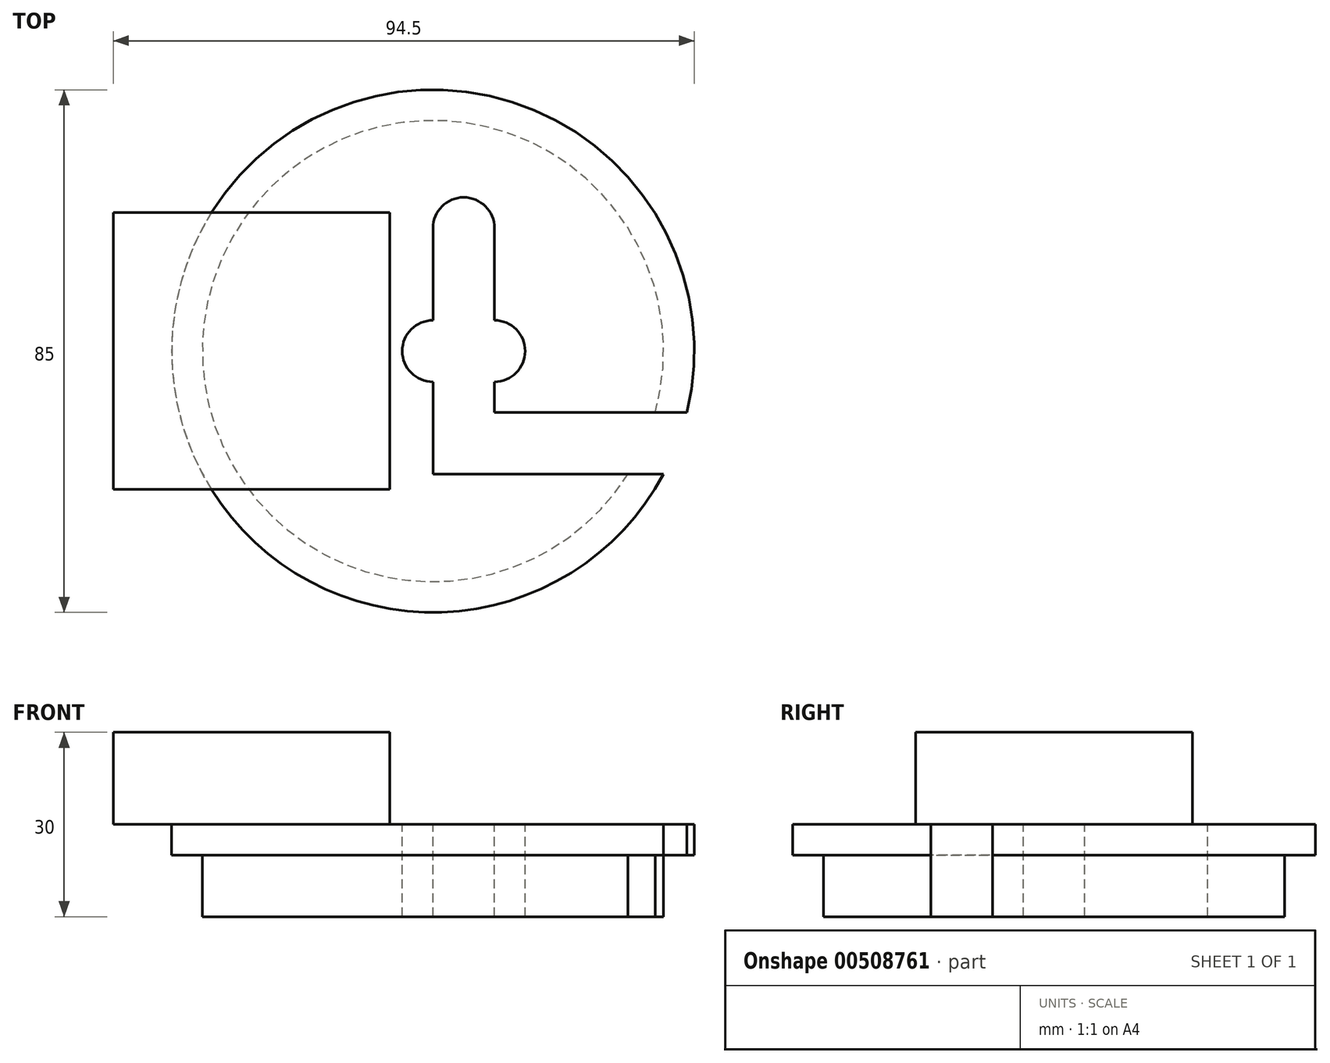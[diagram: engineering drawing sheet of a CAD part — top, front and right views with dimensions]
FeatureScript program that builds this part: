
annotation { "Feature Type Name" : "Feature", "Feature Type Description" : "" }
export const myFeature = defineFeature(function(context is Context, id is Id, definition is map)
    precondition{}
    {
        {
            var Q0;
            Q0=qCreatedBy(makeId("Top.planeOp"),FACE);
            var sketch = newSketch(context, id + "F0", { "sketchPlane" : qUnion([Q0])});
            skArc(sketch, "E0", {"start": v(41.3, -10) * mm, "mid": v(-39.72, 15.12) * mm, "end": v(37.5, -20) * mm});
            skArc(sketch, "E1", {"start": v(0, 5) * mm, "mid": v(-5, 0) * mm, "end": v(0, -5) * mm});
            skLineSegment(sketch, "E2", {"start": v(0, 5) * mm, "end": v(0, 20) * mm});
            skArc(sketch, "E3", {"start": v(10, 20) * mm, "mid": v(5, 25) * mm, "end": v(0, 20) * mm});
            skLineSegment(sketch, "E4", {"start": v(10, 20) * mm, "end": v(10, 5) * mm});
            skArc(sketch, "E5", {"start": v(10, -5) * mm, "mid": v(15, 0) * mm, "end": v(10, 5) * mm});
            skLineSegment(sketch, "E6", {"start": v(10, -5) * mm, "end": v(10, -10) * mm});
            skLineSegment(sketch, "E7", {"start": v(10, -10) * mm, "end": v(41.3, -10) * mm});
            skLineSegment(sketch, "E8", {"start": v(37.5, -20) * mm, "end": v(0, -20) * mm});
            skLineSegment(sketch, "E9", {"start": v(0, -20) * mm, "end": v(0, -5) * mm});
            skLineSegment(sketch, "E10", {"start": v(10, -10) * mm, "end": v(10, -20) * mm, "construction": true});
            skLineSegment(sketch, "E11", {"start": v(10, 20) * mm, "end": v(0, 20) * mm, "construction": true});
            skArc(sketch, "E12", {"start": v(37.5, -20) * mm, "mid": v(39.72, -15.12) * mm, "end": v(41.3, -10) * mm});
            skSolve(sketch);
        }
        {
            var Q0;
            Q0=makeQuery(id+"F0.imprint","IMPRINT",FACE,{"disambiguationData":[TD([[makeQuery(id+"F0.imprint","IMPRINT",EDGE,{"derivedFrom":sQuery(id+"F0.wireOp",EDGE,"E0")}),1.0]])]});
            var Q1;
            Q1=makeQuery(id+"F0.imprint","IMPRINT",FACE,{"disambiguationData":[TD([[makeQuery(id+"F0.imprint","IMPRINT",EDGE,{"derivedFrom":sQuery(id+"F0.wireOp",EDGE,"E1")}),1.0]])]});
            extrude(context, id + "F1", {"entities" : qUnion([Q0, Q1]), "oppositeDirection" : true, "depth" : 5 * mm});
        }
        {
            var Q0;
            Q0=makeQuery(id+"F1.opExtrude","CAP_FACE",FACE,{"disambiguationData":[OSD([sQuery(id+"F0.wireOp",EDGE,"E0"),sQuery(id+"F0.wireOp",EDGE,"E12")])],"isStart":false});
            var sketch = newSketch(context, id + "F2", { "sketchPlane" : qUnion([Q0])});
            skCircle(sketch, "E13", {"center": v(0, 0) * mm, "radius": 37.5 * mm});
            skSolve(sketch);
        }
        {
            var Q0;
            Q0 = qSketchRegion(id + "F2", true);
            extrude(context, id + "F3", {"entities" : qUnion([Q0]), "operationType" : NewBodyOperationType.ADD, "depth" : 10 * mm});
        }
        {
            var Q0;
            Q0=makeQuery(id+"F0.imprint","IMPRINT",FACE,{"disambiguationData":[TD([[makeQuery(id+"F0.imprint","IMPRINT",EDGE,{"derivedFrom":sQuery(id+"F0.wireOp",EDGE,"E1")}),1.0]])]});
            extrude(context, id + "F4", {"entities" : qUnion([Q0]), "operationType" : NewBodyOperationType.REMOVE, "oppositeDirection" : true, "depth" : 40.7 * mm});
        }
        {
            var Q0;
            Q0=makeQuery(id+"F1.opExtrude","CAP_FACE",FACE,{"disambiguationData":[OSD([sQuery(id+"F0.wireOp",EDGE,"E0"),sQuery(id+"F0.wireOp",EDGE,"E12")])],"isStart":true});
            var sketch = newSketch(context, id + "F5", { "sketchPlane" : qUnion([Q0])});
            skLineSegment(sketch, "E14", {"start": v(-7, 22.5) * mm, "end": v(-7, -22.5) * mm});
            skLineSegment(sketch, "E15", {"start": v(0, 0) * mm, "end": v(-7, 0) * mm, "construction": true});
            skLineSegment(sketch, "E16", {"start": v(-7, 22.5) * mm, "end": v(-52, 22.5) * mm});
            skLineSegment(sketch, "E17", {"start": v(-7, -22.5) * mm, "end": v(-52, -22.5) * mm});
            skLineSegment(sketch, "E18", {"start": v(-52, -22.5) * mm, "end": v(-52, 22.5) * mm});
            skSolve(sketch);
        }
        {
            var Q0;
            {var subQ0=sQuery(id+"F5.wireOp",EDGE,"E18");Q0=makeQuery(id+"F5.imprint","IMPRINT",FACE,{"disambiguationData":[TD([[makeQuery(id+"F5.imprint","IMPRINT",EDGE,{"derivedFrom":subQ0}),-1.0]])]});}
            var Q1;
            {var subQ0=sQuery(id+"F5.wireOp",EDGE,"E14");Q1=makeQuery(id+"F5.imprint","IMPRINT",FACE,{"disambiguationData":[TD([[makeQuery(id+"F5.imprint","IMPRINT",EDGE,{"derivedFrom":subQ0}),-1.0]])]});}
            extrude(context, id + "F6", {"entities" : qUnion([Q0, Q1]), "operationType" : NewBodyOperationType.ADD, "depth" : 15 * mm});
        }
    });
